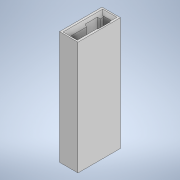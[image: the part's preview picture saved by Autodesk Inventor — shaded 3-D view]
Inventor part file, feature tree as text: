
AUTODESK INVENTOR PART (.ipt)
format: ipt  version: 2020 (Build 240168000, 168)  size: 159,744 bytes
history: native  units: mm
features: move_body x8, direct_edit x3, sketch x3, extrude x2, chamfer x2
ambient origin geometry x8: Origin, YZ Plane, XZ Plane, XY Plane, X Axis, Y Axis, Z Axis, Center Point
bodies: Solid1 (feature_tree)
feature tree (18):
  extrude  "Extrusion1"  Depth=12.0mm
  chamfer  "Chamfer1"  Distance=30.0mm
  direct_edit  "Direct Edit1"
  extrude  "Extrusion2"  TaperAngle=0.0deg  [1 undecoded]
  direct_edit  "Direct Edit2"
  direct_edit  "Direct Edit3"
  chamfer  "Chamfer2"  [1 undecoded]
  sketch  "Sketch3"  dims[d5=1.0mm d6=2.0mm d7=45.0deg d8=0.0mm d9=0.0mm d10=-0.2mm d11=0.0mm d12=0.0mm d13=-0.2mm d14=0.0mm d15=0.0mm d16=-0.25mm d17=0.0mm d18=0.0mm d19=-0.5mm d20=0.0mm d21=0.0mm d22=-0.25mm d23=0.0mm d24=0.0mm d25=-0.5mm d26=2.25mm d27=2.25mm d28=4.5mm d29=0.0mm d30=0.0mm d31=0.0mm d32=0.0mm d33=10.0mm d34=0.0mm d35=0.0mm d36=-0.5mm d37=0.5mm d38=2.0mm d39=45.0deg]
  sketch  "Sketch1"  dims[d0=3.0mm d1=12.0mm]
  sketch  "Sketch2"  dims[d2=2.0mm d3=30.0mm d4=0.0mm]
  move_body  "Move1"
  move_body  "Move2"
  move_body  "Move3"
  move_body  "Move4"
  move_body  "Move5"
  move_body  "Move6"
  move_body  "Move7"
  move_body  "Move8"
note: 2 required parameter values undecoded (feature->parameter linkage not recoverable at this tier; creation-order binding heuristic only, values carry confidence <= 0.55)
